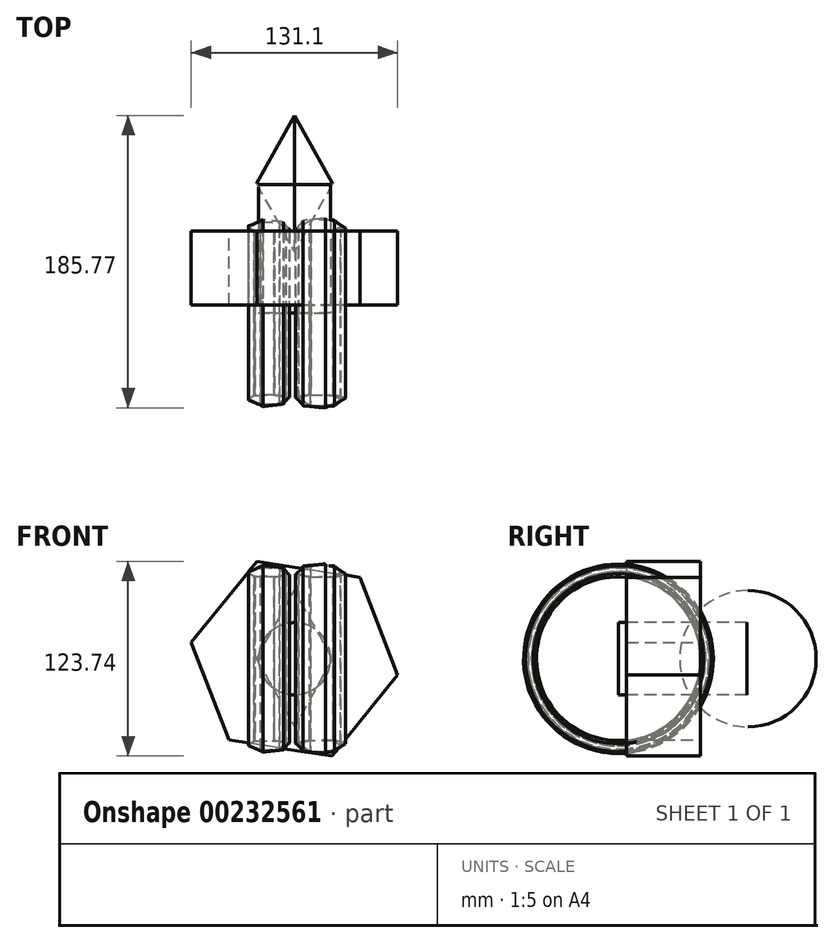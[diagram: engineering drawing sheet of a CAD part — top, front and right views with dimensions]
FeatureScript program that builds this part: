
annotation { "Feature Type Name" : "Feature", "Feature Type Description" : "" }
export const myFeature = defineFeature(function(context is Context, id is Id, definition is map)
    precondition{}
    {
        {
            var Q0;
            Q0=qCreatedBy(makeId("Top.planeOp"),FACE);
            var sketch = newSketch(context, id + "F0", { "sketchPlane" : qUnion([Q0])});
            skLineSegment(sketch, "E0.bottom", {"start": v(0, 29.59) * mm, "end": v(-22.92, 29.59) * mm});
            skLineSegment(sketch, "E0.top", {"start": v(0, -51.97) * mm, "end": v(-22.92, -51.97) * mm});
            skLineSegment(sketch, "E0.left", {"start": v(0, 29.59) * mm, "end": v(0, -51.97) * mm});
            skLineSegment(sketch, "E0.right", {"start": v(-22.92, 29.59) * mm, "end": v(-22.92, -51.97) * mm});
            skSolve(sketch);
        }
        {
            var Q0;
            Q0=makeQuery(id+"F0.imprint","IMPRINT",FACE,{"disambiguationData":[TD([[makeQuery(id+"F0.imprint","IMPRINT",EDGE,{"derivedFrom":sQuery(id+"F0.wireOp",EDGE,"E0.bottom")}),1.0]])]});
            var Q1;
            Q1=sQuery(id+"F0.wireOp",EDGE,"E0.left");
            revolve(context, id + "F1", {"entities" : qUnion([Q0]), "axis" : qUnion([Q1]), "revolveType" : RevolveType.FULL});
        }
        {
            var Q0;
            Q0=makeQuery(id+"F1.opRevolve","SWEPT_FACE",FACE,{"disambiguationData":[OSD([sQuery(id+"F0.wireOp",EDGE,"E0.bottom")])]});
            var Q1;
            Q1=sQuery(id+"F0.wireOp",EDGE,"E0.right");
            sweep(context, id + "F2", {"profiles" : qUnion([Q0]), "path" : qUnion([Q1])});
        }
        {
            var Q0;
            Q0=qCreatedBy(makeId("Front.planeOp"),FACE);
            var sketch = newSketch(context, id + "F3", { "sketchPlane" : qUnion([Q0])});
            skCircle(sketch, "E1.cCircle", {"center": v(17.43, -15.23) * mm, "radius": 12.96 * mm, "construction": true});
            skLineSegment(sketch, "E1.0", {"start": v(32.4, -14.82) * mm, "end": v(25.27, -27.98) * mm});
            skLineSegment(sketch, "E1.1", {"start": v(25.27, -27.98) * mm, "end": v(10.3, -28.39) * mm});
            skLineSegment(sketch, "E1.2", {"start": v(10.3, -28.39) * mm, "end": v(2.47, -15.63) * mm});
            skLineSegment(sketch, "E1.3", {"start": v(2.47, -15.63) * mm, "end": v(9.6, -2.47) * mm});
            skLineSegment(sketch, "E1.4", {"start": v(9.6, -2.47) * mm, "end": v(24.56, -2.07) * mm});
            skLineSegment(sketch, "E1.5", {"start": v(24.56, -2.07) * mm, "end": v(32.4, -14.82) * mm});
            skPoint(sketch, "E1.0.midPoint", {"position": v(28.83, -21.4) * mm});
            skCircle(sketch, "E2.cCircle", {"center": v(-16.28, 15.64) * mm, "radius": 11.59 * mm, "construction": true});
            skLineSegment(sketch, "E2.0", {"start": v(-29.26, 18.92) * mm, "end": v(-19.93, 28.51) * mm});
            skLineSegment(sketch, "E2.1", {"start": v(-19.93, 28.51) * mm, "end": v(-6.96, 25.24) * mm});
            skLineSegment(sketch, "E2.2", {"start": v(-6.96, 25.24) * mm, "end": v(-3.31, 12.37) * mm});
            skLineSegment(sketch, "E2.3", {"start": v(-3.31, 12.37) * mm, "end": v(-12.63, 2.77) * mm});
            skLineSegment(sketch, "E2.4", {"start": v(-12.63, 2.77) * mm, "end": v(-25.6, 6.05) * mm});
            skLineSegment(sketch, "E2.5", {"start": v(-25.6, 6.05) * mm, "end": v(-29.26, 18.92) * mm});
            skPoint(sketch, "E2.0.midPoint", {"position": v(-24.6, 23.72) * mm});
            skCircle(sketch, "E3.cCircle", {"center": v(-17.23, -14.75) * mm, "radius": 10.46 * mm, "construction": true});
            skLineSegment(sketch, "E3.0", {"start": v(-21.47, -26.06) * mm, "end": v(-29.15, -16.74) * mm});
            skLineSegment(sketch, "E3.1", {"start": v(-29.15, -16.74) * mm, "end": v(-24.91, -5.43) * mm});
            skLineSegment(sketch, "E3.2", {"start": v(-24.91, -5.43) * mm, "end": v(-13, -3.44) * mm});
            skLineSegment(sketch, "E3.3", {"start": v(-13, -3.44) * mm, "end": v(-5.32, -12.76) * mm});
            skLineSegment(sketch, "E3.4", {"start": v(-5.32, -12.76) * mm, "end": v(-9.56, -24.07) * mm});
            skLineSegment(sketch, "E3.5", {"start": v(-9.56, -24.07) * mm, "end": v(-21.47, -26.06) * mm});
            skPoint(sketch, "E3.0.midPoint", {"position": v(-25.3, -21.4) * mm});
            skCircle(sketch, "E4.cCircle", {"center": v(15.06, 16.6) * mm, "radius": 12.62 * mm, "construction": true});
            skLineSegment(sketch, "E4.0", {"start": v(19.76, 30.39) * mm, "end": v(29.36, 19.42) * mm});
            skLineSegment(sketch, "E4.1", {"start": v(29.36, 19.42) * mm, "end": v(24.66, 5.62) * mm});
            skLineSegment(sketch, "E4.2", {"start": v(24.66, 5.62) * mm, "end": v(10.36, 2.8) * mm});
            skLineSegment(sketch, "E4.3", {"start": v(10.36, 2.8) * mm, "end": v(0.76, 13.76) * mm});
            skLineSegment(sketch, "E4.4", {"start": v(0.76, 13.76) * mm, "end": v(5.46, 27.56) * mm});
            skLineSegment(sketch, "E4.5", {"start": v(5.46, 27.56) * mm, "end": v(19.76, 30.39) * mm});
            skPoint(sketch, "E4.0.midPoint", {"position": v(24.56, 24.9) * mm});
            skSolve(sketch);
        }
        {
            var Q0;
            Q0=makeQuery(id+"F3.imprint","IMPRINT",FACE,{"disambiguationData":[TD([[makeQuery(id+"F3.imprint","IMPRINT",EDGE,{"derivedFrom":sQuery(id+"F3.wireOp",EDGE,"E1.0")}),-1.0]])]});
            var Q1;
            Q1=makeQuery(id+"F3.imprint","IMPRINT",FACE,{"disambiguationData":[TD([[makeQuery(id+"F3.imprint","IMPRINT",EDGE,{"derivedFrom":sQuery(id+"F3.wireOp",EDGE,"E3.0")}),-1.0]])]});
            var Q2;
            Q2=makeQuery(id+"F3.imprint","IMPRINT",FACE,{"disambiguationData":[TD([[makeQuery(id+"F3.imprint","IMPRINT",EDGE,{"derivedFrom":sQuery(id+"F3.wireOp",EDGE,"E2.0")}),-1.0]])]});
            var Q3;
            Q3=makeQuery(id+"F3.imprint","IMPRINT",FACE,{"disambiguationData":[TD([[makeQuery(id+"F3.imprint","IMPRINT",EDGE,{"derivedFrom":sQuery(id+"F3.wireOp",EDGE,"E4.0")}),-1.0]])]});
            var Q4;
            Q4=sQuery(id+"F0.wireOp",EDGE,"E0.top");
            revolve(context, id + "F4", {"entities" : qUnion([Q0, Q1, Q2, Q3]), "axis" : qUnion([Q4]), "revolveType" : RevolveType.FULL});
        }
        {
            var Q0;
            Q0=qCreatedBy(makeId("Front.planeOp"),FACE);
            var sketch = newSketch(context, id + "F5", { "sketchPlane" : qUnion([Q0])});
            skCircle(sketch, "E5.cCircle", {"center": v(0, 0) * mm, "radius": 57.45 * mm, "construction": true});
            skLineSegment(sketch, "E5.0", {"start": v(-41.6, -51.66) * mm, "end": v(-65.55, 10.2) * mm});
            skLineSegment(sketch, "E5.1", {"start": v(-65.55, 10.2) * mm, "end": v(-23.94, 61.87) * mm});
            skLineSegment(sketch, "E5.2", {"start": v(-23.94, 61.87) * mm, "end": v(41.6, 51.66) * mm});
            skLineSegment(sketch, "E5.3", {"start": v(41.6, 51.66) * mm, "end": v(65.55, -10.2) * mm});
            skLineSegment(sketch, "E5.4", {"start": v(65.55, -10.2) * mm, "end": v(23.94, -61.87) * mm});
            skLineSegment(sketch, "E5.5", {"start": v(23.94, -61.87) * mm, "end": v(-41.6, -51.66) * mm});
            skPoint(sketch, "E5.0.midPoint", {"position": v(-53.58, -20.73) * mm});
            skSolve(sketch);
        }
        {
            var Q0;
            Q0=qCreatedBy(makeId("Top.planeOp"),FACE);
            var sketch = newSketch(context, id + "F6", { "sketchPlane" : qUnion([Q0])});
            skLineSegment(sketch, "E6.0", {"start": v(24.17, 30.24) * mm, "end": v(-24.17, 30.24) * mm});
            skLineSegment(sketch, "E6.1", {"start": v(-24.17, 30.24) * mm, "end": v(0, 73.59) * mm});
            skLineSegment(sketch, "E6.2", {"start": v(0, 73.59) * mm, "end": v(24.17, 30.24) * mm});
            skPoint(sketch, "E6.0.midPoint", {"position": v(0, 30.24) * mm});
            skSolve(sketch);
        }
        {
            var Q0;
            Q0=makeQuery(id+"F6.imprint","IMPRINT",FACE,{"disambiguationData":[TD([[makeQuery(id+"F6.imprint","IMPRINT",EDGE,{"derivedFrom":sQuery(id+"F6.wireOp",EDGE,"E6.0")}),-1.0]])]});
            var Q1;
            Q1=sQuery(id+"F6.wireOp",EDGE,"E6.0");
            revolve(context, id + "F7", {"entities" : qUnion([Q0]), "axis" : qUnion([Q1]), "revolveType" : RevolveType.FULL});
        }
        {
            var Q0;
            Q0=makeQuery(id+"F5.imprint","IMPRINT",FACE,{"disambiguationData":[TD([[makeQuery(id+"F5.imprint","IMPRINT",EDGE,{"derivedFrom":sQuery(id+"F5.wireOp",EDGE,"E5.0")}),-1.0]])]});
            extrude(context, id + "F8", {"entities" : qUnion([Q0]), "depth" : 46.74 * mm});
        }
    });
